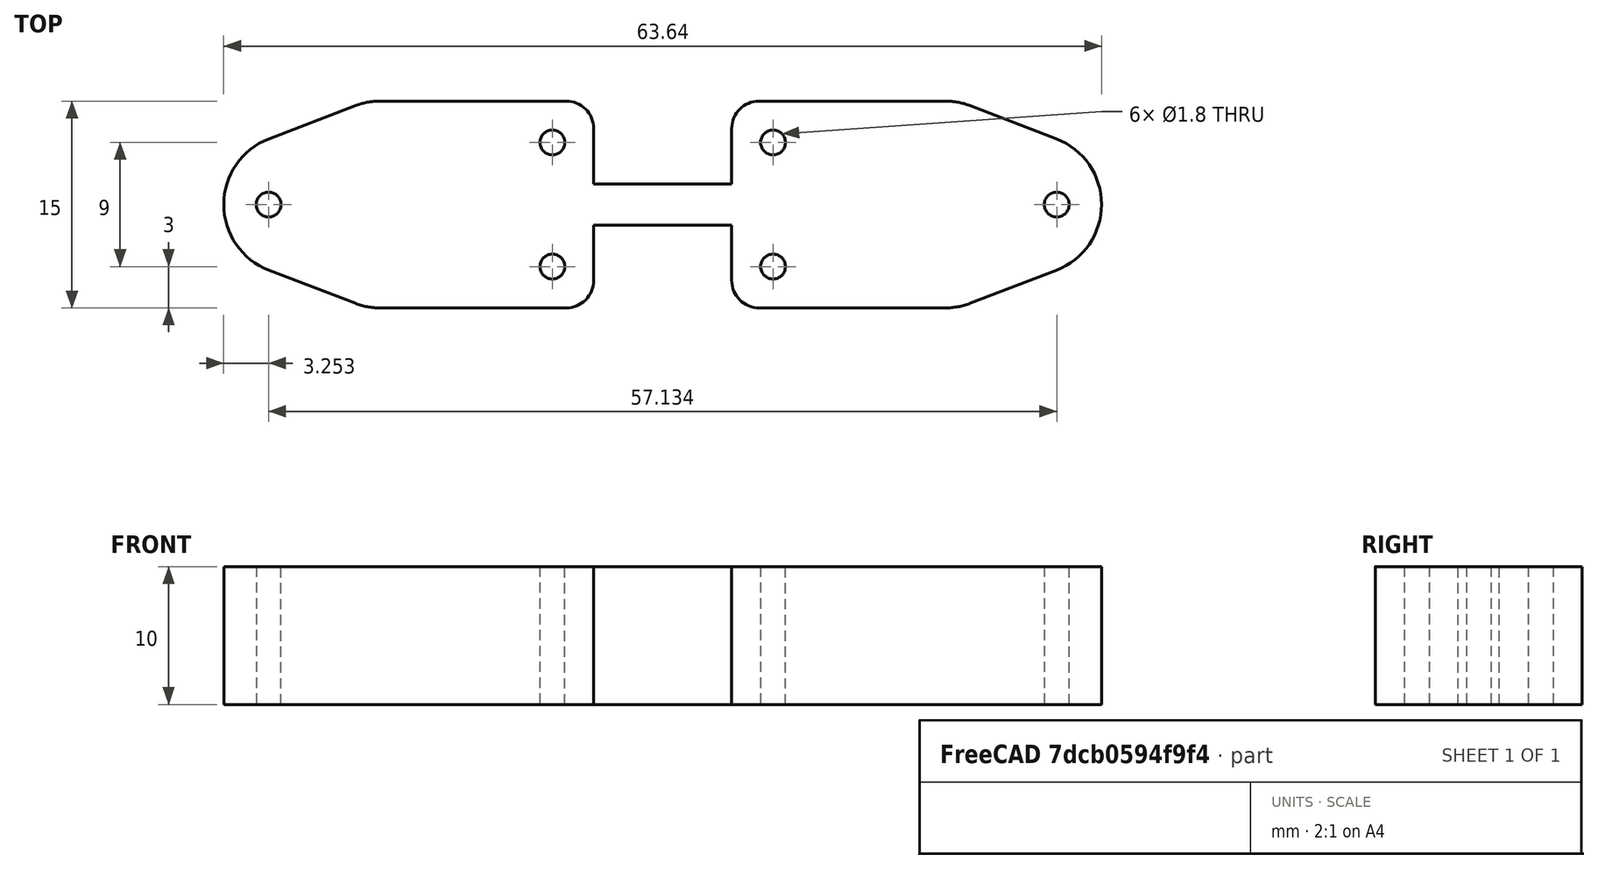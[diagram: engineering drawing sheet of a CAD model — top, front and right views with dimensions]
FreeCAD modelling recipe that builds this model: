
FCSTD DOCUMENT  (FreeCAD 1.2R20251126 (Git shallow))
Label: TT_klicky_pcb
License: All rights reserved
LicenseURL: https://en.wikipedia.org/wiki/All_rights_reserved
objects: App::Point×1, Sketcher::SketchObject×1, PartDesign::Pad×1, PartDesign::Body×1
note: 6 computed .brp shape members not serialized (recipe doc carries the construction recipe); baked Part::Feature solids carry a one-line shape summary decoded from their .brp

FEATURE [App::Point] Origin001  label="原点"
  Role = Origin
FEATURE [Sketcher::SketchObject] Sketch
  ArcFitTolerance = 1e-06
  AttachmentSupport = -> [Origin]
  ExternalTypes = [0]
  FullyConstrained = true
  MakeInternals = false
  MapMode = 5
  sketch-geometry (32):
    g0: ArcOfCircle CenterX=7 CenterY=-5.5 CenterZ=0 NormalX=0 NormalY=0 NormalZ=1 AngleXU=0 Radius=2 StartAngle=3.14159 EndAngle=4.71239
    g1: LineSegment StartX=7 StartY=-7.5 StartZ=0 EndX=20.5 EndY=-7.5 EndZ=0
    g2: ArcOfCircle CenterX=20.5 CenterY=-2.5 CenterZ=0 NormalX=0 NormalY=0 NormalZ=1 AngleXU=0 Radius=5 StartAngle=4.71239 EndAngle=5.0798
    g3: LineSegment StartX=22.296 StartY=-7.16629 StartZ=0 EndX=28.5489 EndY=-4.75962 EndZ=0
    g4: ArcOfCircle CenterX=26.7169 CenterY=0 CenterZ=0 NormalX=0 NormalY=0 NormalZ=1 AngleXU=0 Radius=5.1 StartAngle=5.0798 EndAngle=7.48657
    g5: LineSegment StartX=28.5489 StartY=4.75962 StartZ=0 EndX=22.296 EndY=7.16629 EndZ=0
    g6: ArcOfCircle CenterX=20.5 CenterY=2.5 CenterZ=0 NormalX=0 NormalY=0 NormalZ=1 AngleXU=0 Radius=5 StartAngle=1.20338 EndAngle=1.5708
    g7: LineSegment StartX=20.5 StartY=7.5 StartZ=0 EndX=7 EndY=7.5 EndZ=0
    g8: ArcOfCircle CenterX=7 CenterY=5.5 CenterZ=0 NormalX=0 NormalY=0 NormalZ=1 AngleXU=0 Radius=2 StartAngle=1.5708 EndAngle=3.14159
    g9: Circle CenterX=8 CenterY=4.5 CenterZ=0 NormalX=0 NormalY=0 NormalZ=1 AngleXU=0 Radius=0.9
    g10: Circle CenterX=8 CenterY=-4.5 CenterZ=0 NormalX=0 NormalY=0 NormalZ=1 AngleXU=0 Radius=0.9
    g11: Circle CenterX=28.5669 CenterY=0 CenterZ=0 NormalX=0 NormalY=0 NormalZ=1 AngleXU=0 Radius=0.9
    g12: GeomPoint X=31.8169 Y=0 Z=0
    g13: LineSegment StartX=5 StartY=5.5 StartZ=0 EndX=5 EndY=1.5 EndZ=0
    g14: ArcOfCircle CenterX=-7 CenterY=-5.5 CenterZ=0 NormalX=0 NormalY=0 NormalZ=1 AngleXU=0 Radius=2 StartAngle=4.71239 EndAngle=6.28319
    g15: LineSegment StartX=-7 StartY=-7.5 StartZ=0 EndX=-20.5 EndY=-7.5 EndZ=0
    g16: ArcOfCircle CenterX=-20.5 CenterY=-2.5 CenterZ=0 NormalX=0 NormalY=0 NormalZ=1 AngleXU=0 Radius=5 StartAngle=4.34497 EndAngle=4.71239
    g17: LineSegment StartX=-22.296 StartY=-7.16629 StartZ=0 EndX=-28.5489 EndY=-4.75962 EndZ=0
    g18: ArcOfCircle CenterX=-26.7169 CenterY=0 CenterZ=0 NormalX=0 NormalY=0 NormalZ=1 AngleXU=0 Radius=5.1 StartAngle=1.93821 EndAngle=4.34497
    g19: LineSegment StartX=-28.5489 StartY=4.75962 StartZ=0 EndX=-22.296 EndY=7.16629 EndZ=0
    g20: ArcOfCircle CenterX=-20.5 CenterY=2.5 CenterZ=0 NormalX=0 NormalY=0 NormalZ=1 AngleXU=0 Radius=5 StartAngle=1.5708 EndAngle=1.93821
    g21: LineSegment StartX=-20.5 StartY=7.5 StartZ=0 EndX=-7 EndY=7.5 EndZ=0
    g22: ArcOfCircle CenterX=-7 CenterY=5.5 CenterZ=0 NormalX=0 NormalY=0 NormalZ=1 AngleXU=0 Radius=2 StartAngle=-8e-15 EndAngle=1.5708
    g23: Circle CenterX=-8 CenterY=4.5 CenterZ=0 NormalX=0 NormalY=0 NormalZ=1 AngleXU=0 Radius=0.9
    g24: Circle CenterX=-8 CenterY=-4.5 CenterZ=0 NormalX=0 NormalY=0 NormalZ=1 AngleXU=0 Radius=0.9
    g25: Circle CenterX=-28.5669 CenterY=0 CenterZ=0 NormalX=0 NormalY=0 NormalZ=1 AngleXU=0 Radius=0.9
    g26: GeomPoint X=-31.8169 Y=0 Z=0
    g27: LineSegment StartX=-5 StartY=5.5 StartZ=0 EndX=-5 EndY=1.5 EndZ=0
    g28: LineSegment StartX=-5 StartY=1.5 StartZ=0 EndX=5 EndY=1.5 EndZ=0
    g29: LineSegment StartX=-5 StartY=-1.5 StartZ=0 EndX=5 EndY=-1.5 EndZ=0
    g30: LineSegment StartX=-5 StartY=-1.5 StartZ=0 EndX=-5 EndY=-5.5 EndZ=0
    g31: LineSegment StartX=5 StartY=-1.5 StartZ=0 EndX=5 EndY=-5.5 EndZ=0
  constraints (80):
    c: Tangent(g0,g1) = -1.5708
    c: Tangent(g1,g2) = -1.5708
    c: Tangent(g2,g3) = -1.5708
    c: Tangent(g3,g4) = -1.5708
    c: Tangent(g4,g5) = -1.5708
    c: Tangent(g5,g6) = -1.5708
    c: Tangent(g6,g7) = -1.5708
    c: Tangent(g7,g8) = -1.5708
    c: PointOnObject(g4,g-1)
    c: Equal(g2,g6)
    c: Equal(g8,g0)
    c: Equal(g1,g7)
    c: Equal(g5,g3)
    c: Radius(g8) = 2
    c: DistanceX(g7,g7) = 13.5
    c: Horizontal(g7)
    c: Horizontal(g1)
    c: DistanceY(g0,g7) = 15
    c: Radius(g4) = 5.1
    c: Distance(g5,g5) = 6.7
    c: Radius(g6) = 5
    c: PointOnObject(g11,g-1)
    c: Equal(g11,g9)
    c: Equal(g9,g10)
    c: Diameter(g9) = 1.8
    c: Symmetric(g10,g9,g-1)
    c: Distance(g9,g7) = 3
    c: PointOnObject(g12,g4)
    c: PointOnObject(g12,g-1)
    c: DistanceX(g11,g12) = 3.25
    c: Coincident(g31,g0)
    c: DistanceX(g0,g10) = 3
    c: Symmetric(g0,g8,g-1)
    c: Tangent(g13,g8) = -1.5708
    c: Tangent(g14,g15) = 1.5708
    c: Tangent(g15,g16) = 1.5708
    c: Tangent(g16,g17) = 1.5708
    c: Tangent(g17,g18) = 1.5708
    c: Tangent(g18,g19) = 1.5708
    c: Tangent(g19,g20) = 1.5708
    c: Tangent(g20,g21) = 1.5708
    c: Tangent(g21,g22) = 1.5708
    c: Equal(g16,g20)
    c: Equal(g22,g14)
    c: Equal(g15,g21)
    c: Equal(g19,g17)
    c: Radius(g22) = 2
    c: Horizontal(g21)
    c: Horizontal(g15)
    c: Radius(g18) = 5.1
    c: Distance(g19,g19) = 6.7
    c: Radius(g20) = 5
    c: Equal(g25,g23)
    c: Equal(g23,g24)
    c: Diameter(g23) = 1.8
    c: Distance(g23,g21) = 3
    c: PointOnObject(g26,g18)
    c: Tangent(g27,g22) = 1.5708
    c: DistanceX(g21,g21) = 13.5
    c: Distance(g24,g15) = 3
    c: Distance(g25,g26) = 3.25
    c: Symmetric(g23,g24,g-1)
    c: PointOnObject(g18,g-1)
    c: PointOnObject(g25,g-1)
    c: DistanceY(g14,g21) = 15
    c: Tangent(g30,g14) = 1.5708
    c: PointOnObject(g26,g-1)
    c: DistanceX(g22,g-1) = 5
    c: Horizontal(g29)
    c: Symmetric(g28,g29,g-1)
    c: Distance(g24,g30) = 3
    c: Coincident(g28,g27)
    c: Coincident(g30,g29)
    c: Coincident(g28,g13)
    c: Coincident(g29,g31)
    c: Distance(g29,g28) = 3
    c: Symmetric(g27,g13,g-2)
    c: Perpendicular(g28,g13)
    c: Perpendicular(g28,g27)
    c: Equal(g29,g28)
FEATURE [PartDesign::Pad] Pad
  Direction = (0,0,1)
  Length = 10
  Length2 = 10
  Profile = -> Sketch
  ReferenceAxis = -> Sketch [N_Axis]
  Refine = true
  SideType = 0
  Suppressed = false
  Type = 0
  Type2 = 0
FEATURE [PartDesign::Body] Body
  AllowCompound = true
  Group = -> [Sketch,Pad]
  Origin = -> Origin
  Tip = -> Pad
